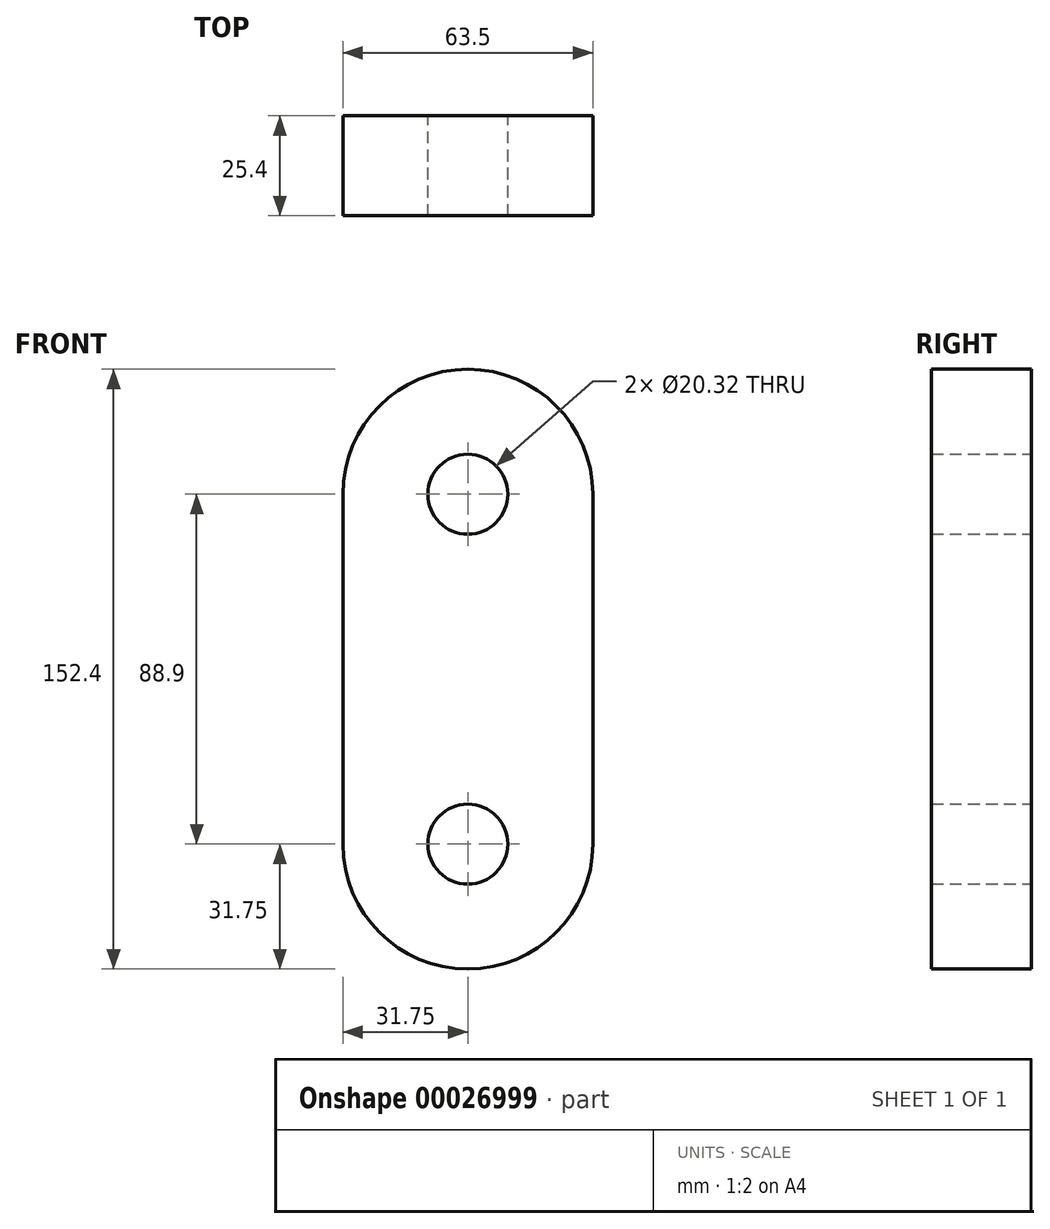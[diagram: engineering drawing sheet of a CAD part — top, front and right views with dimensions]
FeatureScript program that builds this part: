
annotation { "Feature Type Name" : "Feature", "Feature Type Description" : "" }
export const myFeature = defineFeature(function(context is Context, id is Id, definition is map)
    precondition{}
    {
        {
            var Q0;
            Q0=qCreatedBy(makeId("Front.planeOp"),FACE);
            var sketch = newSketch(context, id + "F0", { "sketchPlane" : qUnion([Q0])});
            skCircle(sketch, "E0", {"center": v(31.75, -31.75) * mm, "radius": 31.75 * mm});
            skCircle(sketch, "E1", {"center": v(31.75, -273.05) * mm, "radius": 31.75 * mm});
            skLineSegment(sketch, "E2", {"start": v(0, -184.15) * mm, "end": v(0, -273.05) * mm});
            skLineSegment(sketch, "E3", {"start": v(63.5, -184.15) * mm, "end": v(63.5, -273.05) * mm});
            skCircle(sketch, "E4", {"center": v(31.75, -273.05) * mm, "radius": 10.16 * mm});
            skCircle(sketch, "E5", {"center": v(31.75, -31.75) * mm, "radius": 10.16 * mm});
            skLineSegment(sketch, "E6", {"start": v(63.5, -184.15) * mm, "end": v(0, -184.15) * mm});
            skCircle(sketch, "E7", {"center": v(31.75, -184.15) * mm, "radius": 31.75 * mm});
            skCircle(sketch, "E8", {"center": v(31.75, -184.15) * mm, "radius": 10.16 * mm});
            skSolve(sketch);
        }
        {
            var Q0;
            {var subQ1=sQuery(id+"F0.wireOp",EDGE,"E2");Q0=makeQuery(id+"F0.imprint","IMPRINT",FACE,{"disambiguationData":[TD([[makeQuery(id+"F0.imprint","IMPRINT",EDGE,{"derivedFrom":subQ1}),1.0]])]});}
            var Q1;
            Q1=makeQuery(id+"F0.imprint","IMPRINT",FACE,{"disambiguationData":[TD([[makeQuery(id+"F0.imprint","IMPRINT",EDGE,{"derivedFrom":sQuery(id+"F0.wireOp",EDGE,"E4")}),-1.0]])]});
            var Q2;
            {var subQ0=sQuery(id+"F0.wireOp",EDGE,"E8");var subQ1=sQuery(id+"F0.wireOp",EDGE,"E6");var subQ3=makeQuery(id+"F0.imprint","INTERSECT",VERTEX,{"disambiguationData":[OD(0.0)],"derivedFrom":[subQ1,subQ0]});Q2=makeQuery(id+"F0.imprint","IMPRINT",FACE,{"disambiguationData":[TD([[makeQuery(id+"F0.imprint","IMPRINT",EDGE,{"disambiguationData":[TD([[subQ3,-1.0]])],"derivedFrom":subQ0}),-1.0]])]});}
            var Q3;
            {var subQ0=sQuery(id+"F0.wireOp",EDGE,"E8");var subQ1=sQuery(id+"F0.wireOp",EDGE,"E6");var subQ3=makeQuery(id+"F0.imprint","INTERSECT",VERTEX,{"disambiguationData":[OD(0.0)],"derivedFrom":[subQ1,subQ0]});Q3=makeQuery(id+"F0.imprint","IMPRINT",FACE,{"disambiguationData":[TD([[makeQuery(id+"F0.imprint","IMPRINT",EDGE,{"disambiguationData":[TD([[subQ3,1.0]])],"derivedFrom":subQ0}),-1.0]])]});}
            extrude(context, id + "F1", {"entities" : qUnion([Q0, Q1, Q2, Q3]), "endBound" : BoundingType.SYMMETRIC, "depth" : 25.4 * mm});
        }
    });
